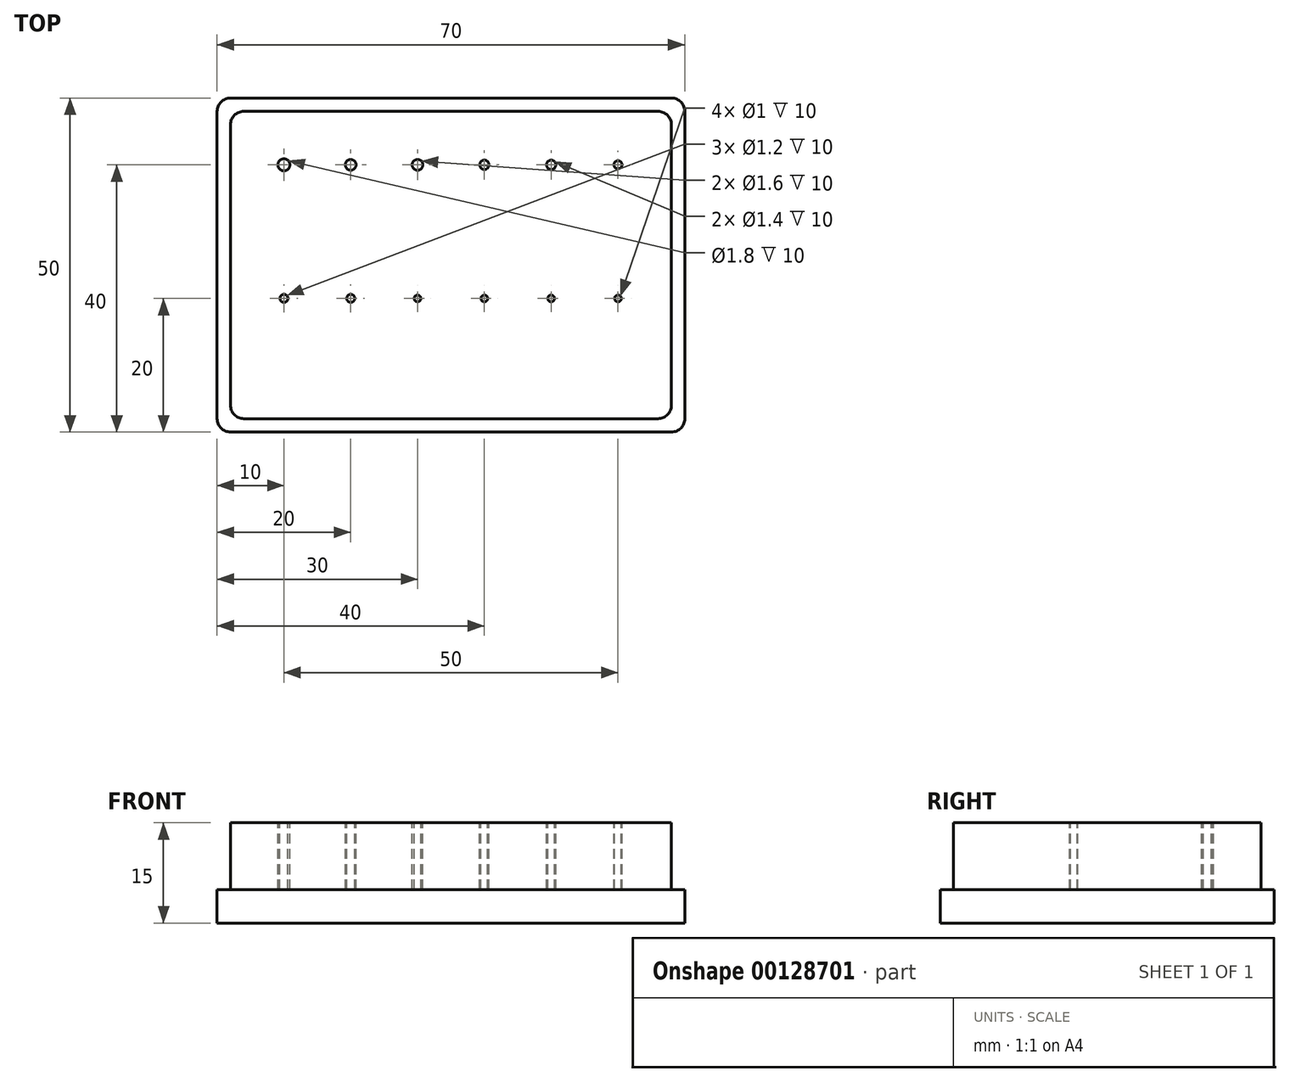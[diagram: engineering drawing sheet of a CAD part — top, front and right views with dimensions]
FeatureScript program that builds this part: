
annotation { "Feature Type Name" : "Feature", "Feature Type Description" : "" }
export const myFeature = defineFeature(function(context is Context, id is Id, definition is map)
    precondition{}
    {
        {
            var Q0;
            Q0=qCreatedBy(makeId("Top.planeOp"),FACE);
            var sketch = newSketch(context, id + "F0", { "sketchPlane" : qUnion([Q0])});
            skLineSegment(sketch, "E0.bottom", {"start": v(-35, 25) * mm, "end": v(35, 25) * mm});
            skLineSegment(sketch, "E0.top", {"start": v(-35, -25) * mm, "end": v(35, -25) * mm});
            skLineSegment(sketch, "E0.left", {"start": v(-35, 25) * mm, "end": v(-35, -25) * mm});
            skLineSegment(sketch, "E0.right", {"start": v(35, 25) * mm, "end": v(35, -25) * mm});
            skPoint(sketch, "E0.middle", {"position": v(0, 0) * mm});
            skSolve(sketch);
        }
        {
            var Q0;
            Q0 = qSketchRegion(id + "F0", true);
            extrude(context, id + "F1", {"entities" : qUnion([Q0]), "depth" : 5 * mm});
        }
        {
            var Q0;
            Q0=makeQuery(id+"F1.opExtrude","CAP_FACE",FACE,{"disambiguationData":[OSD([sQuery(id+"F0.wireOp",EDGE,"E0.bottom"),sQuery(id+"F0.wireOp",EDGE,"E0.top"),sQuery(id+"F0.wireOp",EDGE,"E0.left"),sQuery(id+"F0.wireOp",EDGE,"E0.right")])],"isStart":false});
            var sketch = newSketch(context, id + "F2", { "sketchPlane" : qUnion([Q0])});
            skLineSegment(sketch, "E1.0", {"start": v(-35, 25) * mm, "end": v(35, 25) * mm, "construction": true});
            skLineSegment(sketch, "E1.1", {"start": v(-35, 25) * mm, "end": v(-35, -25) * mm, "construction": true});
            skLineSegment(sketch, "E1.2", {"start": v(-35, -25) * mm, "end": v(35, -25) * mm, "construction": true});
            skLineSegment(sketch, "E1.3", {"start": v(35, 25) * mm, "end": v(35, -25) * mm, "construction": true});
            skLineSegment(sketch, "E2.0", {"start": v(-33, 23) * mm, "end": v(33, 23) * mm});
            skLineSegment(sketch, "E2.1", {"start": v(-33, 23) * mm, "end": v(-33, -23) * mm});
            skLineSegment(sketch, "E2.2", {"start": v(-33, -23) * mm, "end": v(33, -23) * mm});
            skLineSegment(sketch, "E2.3", {"start": v(33, 23) * mm, "end": v(33, -23) * mm});
            skSolve(sketch);
        }
        {
            var Q0;
            Q0=makeQuery(id+"F2.imprint","IMPRINT",FACE,{"disambiguationData":[TD([[makeQuery(id+"F2.imprint","IMPRINT",EDGE,{"derivedFrom":sQuery(id+"F2.wireOp",EDGE,"E2.0")}),-1.0]])]});
            extrude(context, id + "F3", {"entities" : qUnion([Q0]), "operationType" : NewBodyOperationType.ADD, "depth" : 10 * mm});
        }
        {
            var Q0;
            Q0=makeQuery(id+"F3.opExtrude","SWEPT_EDGE",EDGE,{"disambiguationData":[OSD([sQuery(id+"F2.wireOp",EDGE,"E2.1"),sQuery(id+"F2.wireOp",EDGE,"E2.2")])]});
            var Q1;
            Q1=makeQuery(id+"F3.opExtrude","SWEPT_EDGE",EDGE,{"disambiguationData":[OSD([sQuery(id+"F2.wireOp",EDGE,"E2.2"),sQuery(id+"F2.wireOp",EDGE,"E2.3")])]});
            var Q2;
            Q2=makeQuery(id+"F1.opExtrude","SWEPT_EDGE",EDGE,{"disambiguationData":[OSD([sQuery(id+"F0.wireOp",EDGE,"E0.top"),sQuery(id+"F0.wireOp",EDGE,"E0.right")])]});
            var Q3;
            Q3=makeQuery(id+"F1.opExtrude","SWEPT_EDGE",EDGE,{"disambiguationData":[OSD([sQuery(id+"F0.wireOp",EDGE,"E0.top"),sQuery(id+"F0.wireOp",EDGE,"E0.left")])]});
            var Q4;
            Q4=makeQuery(id+"F1.opExtrude","SWEPT_EDGE",EDGE,{"disambiguationData":[OSD([sQuery(id+"F0.wireOp",EDGE,"E0.bottom"),sQuery(id+"F0.wireOp",EDGE,"E0.left")])]});
            var Q5;
            Q5=makeQuery(id+"F3.opExtrude","SWEPT_EDGE",EDGE,{"disambiguationData":[OSD([sQuery(id+"F2.wireOp",EDGE,"E2.0"),sQuery(id+"F2.wireOp",EDGE,"E2.1")])]});
            var Q6;
            Q6=makeQuery(id+"F3.opExtrude","SWEPT_EDGE",EDGE,{"disambiguationData":[OSD([sQuery(id+"F2.wireOp",EDGE,"E2.0"),sQuery(id+"F2.wireOp",EDGE,"E2.3")])]});
            var Q7;
            Q7=makeQuery(id+"F1.opExtrude","SWEPT_EDGE",EDGE,{"disambiguationData":[OSD([sQuery(id+"F0.wireOp",EDGE,"E0.bottom"),sQuery(id+"F0.wireOp",EDGE,"E0.right")])]});
            fillet(context, id + "F4", {"entities" : qUnion([Q0, Q1, Q2, Q3, Q4, Q5, Q6, Q7]), "radius" : 2 * mm, "tangentPropagation" : true, "allowEdgeOverflow" : false});
        }
        {
            var Q0;
            Q0=makeQuery(id+"F3.opExtrude","CAP_FACE",FACE,{"disambiguationData":[OSD([sQuery(id+"F2.wireOp",EDGE,"E2.0"),sQuery(id+"F2.wireOp",EDGE,"E2.1"),sQuery(id+"F2.wireOp",EDGE,"E2.2"),sQuery(id+"F2.wireOp",EDGE,"E2.3")])],"isStart":false});
            var sketch = newSketch(context, id + "F5", { "sketchPlane" : qUnion([Q0])});
            skPoint(sketch, "E3", {"position": v(-25, 15) * mm});
            skPoint(sketch, "E4.0.1.0", {"position": v(-25, -5) * mm});
            skPoint(sketch, "E4.1.0.0", {"position": v(-15, 15) * mm});
            skPoint(sketch, "E4.1.1.0", {"position": v(-15, -5) * mm});
            skPoint(sketch, "E4.2.0.0", {"position": v(-5, 15) * mm});
            skPoint(sketch, "E4.2.1.0", {"position": v(-5, -5) * mm});
            skPoint(sketch, "E4.3.0.0", {"position": v(5, 15) * mm});
            skPoint(sketch, "E4.3.1.0", {"position": v(5, -5) * mm});
            skPoint(sketch, "E4.4.0.0", {"position": v(15, 15) * mm});
            skPoint(sketch, "E4.4.1.0", {"position": v(15, -5) * mm});
            skPoint(sketch, "E4.5.0.0", {"position": v(25, 15) * mm});
            skPoint(sketch, "E4.5.1.0", {"position": v(25, -5) * mm});
            skLineSegment(sketch, "E4.direction1", {"start": v(-25, 15) * mm, "end": v(-15, 15) * mm, "construction": true});
            skLineSegment(sketch, "E4.direction2", {"start": v(-25, 15) * mm, "end": v(-25, -5) * mm, "construction": true});
            skCircle(sketch, "E5", {"center": v(25, -5) * mm, "radius": 0.5 * mm});
            skCircle(sketch, "E6", {"center": v(15, -5) * mm, "radius": 0.5 * mm});
            skCircle(sketch, "E7", {"center": v(5, -5) * mm, "radius": 0.5 * mm});
            skCircle(sketch, "E8", {"center": v(-5, -5) * mm, "radius": 0.5 * mm});
            skCircle(sketch, "E9", {"center": v(-15, -5) * mm, "radius": 0.6 * mm});
            skCircle(sketch, "E10", {"center": v(-25, -5) * mm, "radius": 0.6 * mm});
            skCircle(sketch, "E11", {"center": v(25, 15) * mm, "radius": 0.6 * mm});
            skCircle(sketch, "E12", {"center": v(15, 15) * mm, "radius": 0.7 * mm});
            skCircle(sketch, "E13", {"center": v(5, 15) * mm, "radius": 0.7 * mm});
            skCircle(sketch, "E14", {"center": v(-5, 15) * mm, "radius": 0.8 * mm});
            skCircle(sketch, "E15", {"center": v(-15, 15) * mm, "radius": 0.8 * mm});
            skCircle(sketch, "E16", {"center": v(-25, 15) * mm, "radius": 0.9 * mm});
            skSolve(sketch);
        }
        {
            var Q0;
            Q0 = qSketchRegion(id + "F5", true);
            extrude(context, id + "F6", {"entities" : qUnion([Q0]), "operationType" : NewBodyOperationType.REMOVE, "oppositeDirection" : true, "depth" : 10 * mm});
        }
    });
